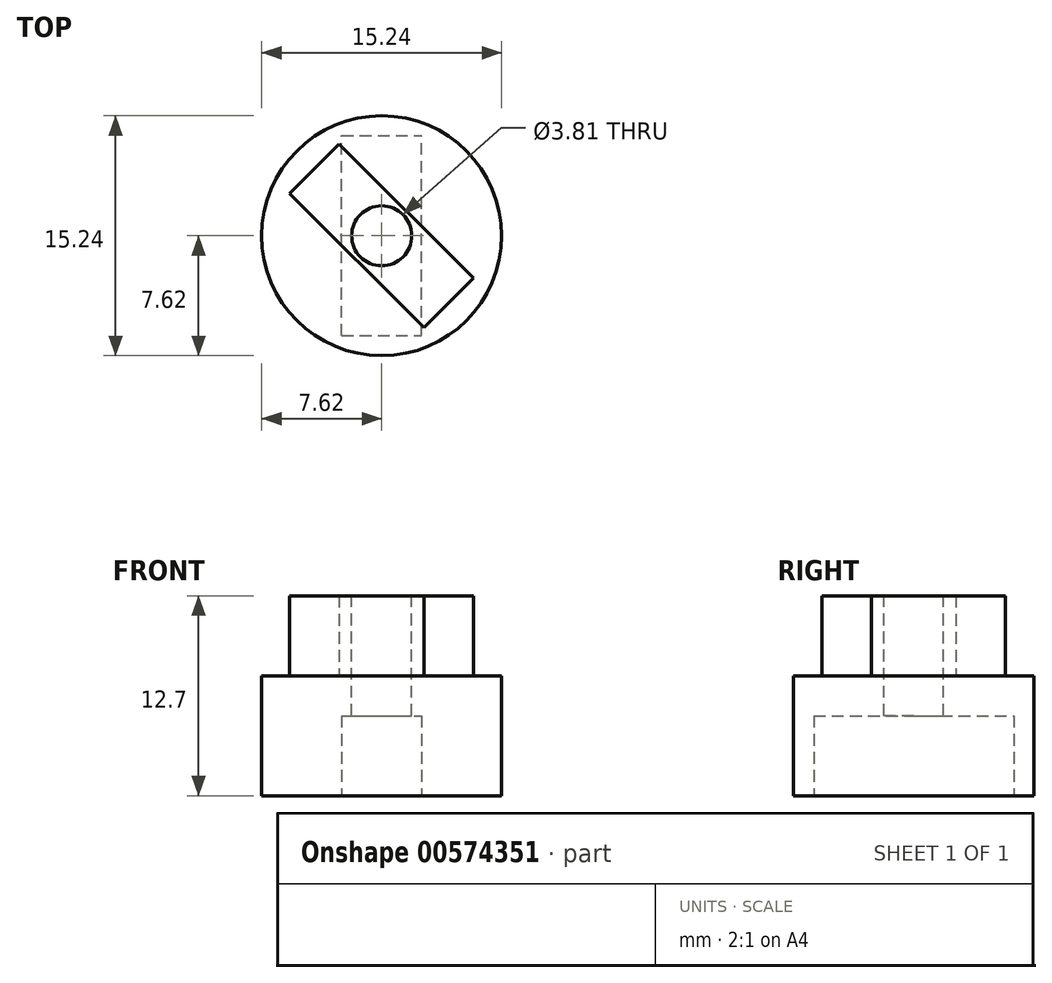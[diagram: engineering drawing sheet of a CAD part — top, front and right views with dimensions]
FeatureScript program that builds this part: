
annotation { "Feature Type Name" : "Feature", "Feature Type Description" : "" }
export const myFeature = defineFeature(function(context is Context, id is Id, definition is map)
    precondition{}
    {
        {
            var Q0;
            Q0=qCreatedBy(makeId("Top.planeOp"),FACE);
            var sketch = newSketch(context, id + "F0", { "sketchPlane" : qUnion([Q0])});
            skCircle(sketch, "E0", {"center": v(0, 0) * mm, "radius": 7.62 * mm});
            skSolve(sketch);
        }
        {
            var Q0;
            Q0 = qSketchRegion(id + "F0", true);
            extrude(context, id + "F1", {"entities" : qUnion([Q0]), "depth" : 7.62 * mm, "offsetDistance" : 25.4 * mm});
        }
        {
            var Q0;
            Q0=makeQuery(id+"F1.opExtrude","CAP_FACE",FACE,{"disambiguationData":[OSD([sQuery(id+"F0.wireOp",EDGE,"E0")])],"isStart":true});
            var sketch = newSketch(context, id + "F2", { "sketchPlane" : qUnion([Q0])});
            skLineSegment(sketch, "E1.bottom", {"start": v(-2.54, 6.35) * mm, "end": v(2.54, 6.35) * mm});
            skLineSegment(sketch, "E1.top", {"start": v(-2.54, -6.35) * mm, "end": v(2.54, -6.35) * mm});
            skLineSegment(sketch, "E1.left", {"start": v(-2.54, 6.35) * mm, "end": v(-2.54, -6.35) * mm});
            skLineSegment(sketch, "E1.right", {"start": v(2.54, 6.35) * mm, "end": v(2.54, -6.35) * mm});
            skLineSegment(sketch, "E2", {"start": v(0, 6.35) * mm, "end": v(0, 0) * mm, "construction": true});
            skLineSegment(sketch, "E3", {"start": v(-2.54, 0) * mm, "end": v(0, 0) * mm, "construction": true});
            skSolve(sketch);
        }
        {
            var Q0;
            Q0=makeQuery(id+"F2.imprint","IMPRINT",FACE,{"disambiguationData":[TD([[makeQuery(id+"F2.imprint","IMPRINT",EDGE,{"derivedFrom":sQuery(id+"F2.wireOp",EDGE,"E1.bottom")}),-1.0]])]});
            extrude(context, id + "F3", {"entities" : qUnion([Q0]), "operationType" : NewBodyOperationType.REMOVE, "oppositeDirection" : true, "depth" : 5.08 * mm, "offsetDistance" : 25.4 * mm});
        }
        {
            var Q0;
            Q0=makeQuery(id+"F1.opExtrude","CAP_FACE",FACE,{"disambiguationData":[OSD([sQuery(id+"F0.wireOp",EDGE,"E0")])],"isStart":false});
            var sketch = newSketch(context, id + "F4", { "sketchPlane" : qUnion([Q0])});
            skLineSegment(sketch, "E4", {"start": v(-5.84, 2.7) * mm, "end": v(2.7, -5.84) * mm});
            skLineSegment(sketch, "E5", {"start": v(2.7, -5.84) * mm, "end": v(5.84, -2.7) * mm});
            skLineSegment(sketch, "E6", {"start": v(5.84, -2.7) * mm, "end": v(-2.7, 5.84) * mm});
            skLineSegment(sketch, "E7", {"start": v(-2.7, 5.84) * mm, "end": v(-5.84, 2.7) * mm});
            skLineSegment(sketch, "E8", {"start": v(0, 0) * mm, "end": v(-4.27, 4.27) * mm, "construction": true});
            skLineSegment(sketch, "E9", {"start": v(0, 0) * mm, "end": v(-1.57, -1.57) * mm, "construction": true});
            skLineSegment(sketch, "E10", {"start": v(0, 0) * mm, "end": v(0, 7.62) * mm, "construction": true});
            skSolve(sketch);
        }
        {
            var Q0;
            Q0=makeQuery(id+"F4.imprint","IMPRINT",FACE,{"disambiguationData":[TD([[makeQuery(id+"F4.imprint","IMPRINT",EDGE,{"derivedFrom":sQuery(id+"F4.wireOp",EDGE,"E4")}),1.0]])]});
            extrude(context, id + "F5", {"entities" : qUnion([Q0]), "operationType" : NewBodyOperationType.ADD, "depth" : 5.08 * mm, "offsetDistance" : 25.4 * mm});
        }
        {
            var Q0;
            Q0=makeQuery(id+"F5.opExtrude","CAP_FACE",FACE,{"disambiguationData":[OSD([sQuery(id+"F4.wireOp",EDGE,"E4"),sQuery(id+"F4.wireOp",EDGE,"E5"),sQuery(id+"F4.wireOp",EDGE,"E6"),sQuery(id+"F4.wireOp",EDGE,"E7")])],"isStart":false});
            var sketch = newSketch(context, id + "F6", { "sketchPlane" : qUnion([Q0])});
            skCircle(sketch, "E11", {"center": v(0, 0) * mm, "radius": 1.9 * mm});
            skSolve(sketch);
        }
        {
            var Q0;
            Q0 = qSketchRegion(id + "F6", true);
            extrude(context, id + "F7", {"entities" : qUnion([Q0]), "operationType" : NewBodyOperationType.REMOVE, "endBound" : BoundingType.THROUGH_ALL, "oppositeDirection" : true, "depth" : 25.4 * mm, "offsetDistance" : 25.4 * mm});
        }
    });
